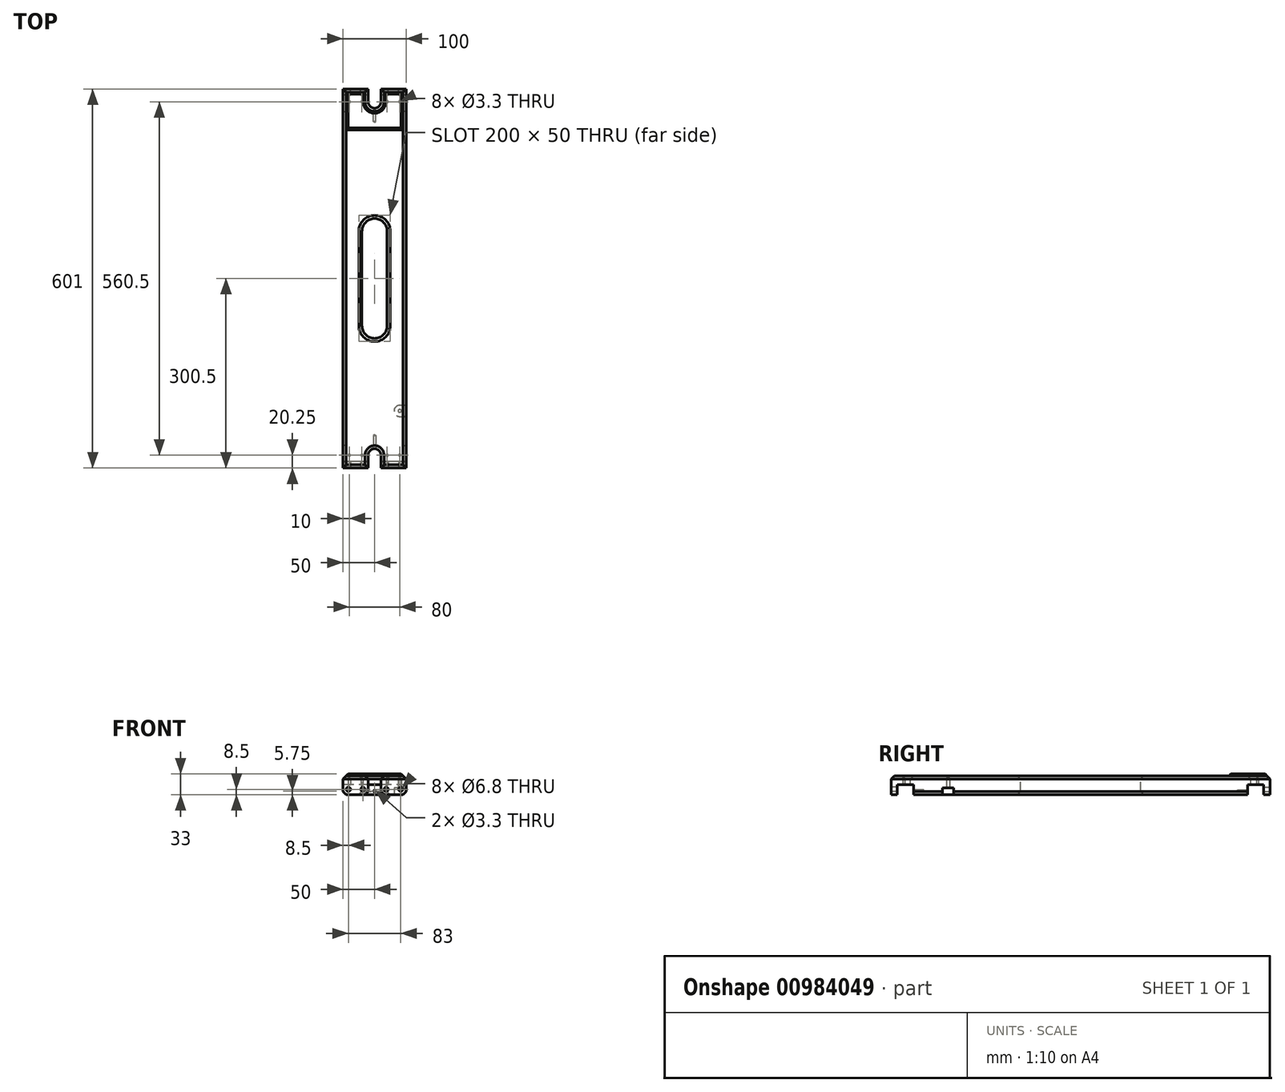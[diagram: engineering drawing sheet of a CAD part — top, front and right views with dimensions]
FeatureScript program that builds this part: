
annotation { "Feature Type Name" : "Feature", "Feature Type Description" : "" }
export const myFeature = defineFeature(function(context is Context, id is Id, definition is map)
    precondition{}
    {
        {
            var Q0;
            Q0=qCreatedBy(makeId("Right.planeOp"),FACE);
            var sketch = newSketch(context, id + "F0", { "sketchPlane" : qUnion([Q0])});
            skLineSegment(sketch, "E0", {"start": v(-300.5, -30) * mm, "end": v(-290.5, -30) * mm});
            skLineSegment(sketch, "E1", {"start": v(-290.5, -30) * mm, "end": v(-290.5, -14) * mm});
            skLineSegment(sketch, "E2", {"start": v(265, -30) * mm, "end": v(265, -14) * mm});
            skLineSegment(sketch, "E3", {"start": v(265, -14) * mm, "end": v(290.5, -14) * mm});
            skLineSegment(sketch, "E4", {"start": v(290.5, -14) * mm, "end": v(290.5, -30) * mm});
            skLineSegment(sketch, "E5", {"start": v(290.5, -30) * mm, "end": v(300.5, -30) * mm});
            skLineSegment(sketch, "E6", {"start": v(300.5, -30) * mm, "end": v(300.5, 0) * mm});
            skLineSegment(sketch, "E7", {"start": v(300.5, 0) * mm, "end": v(-300.5, 0) * mm});
            skLineSegment(sketch, "E8", {"start": v(-300.5, 0) * mm, "end": v(-300.5, -30) * mm});
            skLineSegment(sketch, "E9", {"start": v(-290.5, -14) * mm, "end": v(-265, -14) * mm});
            skLineSegment(sketch, "E10", {"start": v(-265, -14) * mm, "end": v(-265, -30) * mm});
            skLineSegment(sketch, "E11", {"start": v(-265, -30) * mm, "end": v(265, -30) * mm});
            skSolve(sketch);
        }
        {
            var Q0;
            Q0=makeQuery(id+"F0.imprint","IMPRINT",FACE,{"disambiguationData":[TD([[makeQuery(id+"F0.imprint","IMPRINT",EDGE,{"derivedFrom":sQuery(id+"F0.wireOp",EDGE,"E0")}),1.0]])]});
            extrude(context, id + "F1", {"entities" : qUnion([Q0]), "depth" : 100 * mm, "offsetDistance" : 25 * mm, "symmetric" : true});
        }
        {
            var Q0;
            {var subQ0=sQuery(id+"F0.wireOp",EDGE,"E7");Q0=makeQuery(id+"F2rq3QJmj17pkRO_1.boolean.opBoolean","MERGE",FACE,{"derivedFrom":[makeQuery(id+"F1.opExtrude","SWEPT_FACE",FACE,{"disambiguationData":[OSD([subQ0])]}),makeQuery(id+"F2rq3QJmj17pkRO_1.opExtrude","SWEPT_FACE",FACE,{"disambiguationData":[OSD([subQ0]),TDD([makeQuery(id+"F0.imprint","IMPRINT",EDGE,{"disambiguationData":[TD([[makeQuery(id+"F0.imprint","INTERSECT",VERTEX,{"derivedFrom":[sQuery(id+"F0.wireOp",EDGE,"E6"),subQ0]}),-1.0]])],"derivedFrom":subQ0})])]}),makeQuery(id+"F2rq3QJmj17pkRO_1.opExtrude","SWEPT_FACE",FACE,{"disambiguationData":[OSD([subQ0]),TDD([makeQuery(id+"F0.imprint","IMPRINT",EDGE,{"disambiguationData":[TD([[makeQuery(id+"F0.imprint","INTERSECT",VERTEX,{"derivedFrom":[subQ0,sQuery(id+"F0.wireOp",EDGE,"E8")]}),1.0]])],"derivedFrom":subQ0})])]})]});}
            var sketch = newSketch(context, id + "F2", { "sketchPlane" : qUnion([Q0])});
            skLineSegment(sketch, "E12.bottom", {"start": v(20, -75) * mm, "end": v(-20, -75) * mm});
            skLineSegment(sketch, "E12.top", {"start": v(20, 75) * mm, "end": v(-20, 75) * mm});
            skLineSegment(sketch, "E12.left", {"start": v(20, -75) * mm, "end": v(20, 75) * mm});
            skLineSegment(sketch, "E12.right", {"start": v(-20, -75) * mm, "end": v(-20, 75) * mm});
            skPoint(sketch, "E12.middle", {"position": v(0, 0) * mm});
            skCircle(sketch, "E13", {"center": v(0, 280) * mm, "radius": 10 * mm});
            skCircle(sketch, "E14", {"center": v(0, -280) * mm, "radius": 10 * mm});
            skLineSegment(sketch, "E15.bottom", {"start": v(-10, -280) * mm, "end": v(10, -280) * mm});
            skLineSegment(sketch, "E15.top", {"start": v(-10, -300.5) * mm, "end": v(10, -300.5) * mm});
            skLineSegment(sketch, "E15.left", {"start": v(-10, -280) * mm, "end": v(-10, -300.5) * mm});
            skLineSegment(sketch, "E15.right", {"start": v(10, -280) * mm, "end": v(10, -300.5) * mm});
            skLineSegment(sketch, "E16.bottom", {"start": v(-10, 280) * mm, "end": v(10, 280) * mm});
            skLineSegment(sketch, "E16.top", {"start": v(-10, 300.5) * mm, "end": v(10, 300.5) * mm});
            skLineSegment(sketch, "E16.left", {"start": v(-10, 280) * mm, "end": v(-10, 300.5) * mm});
            skLineSegment(sketch, "E16.right", {"start": v(10, 280) * mm, "end": v(10, 300.5) * mm});
            skCircle(sketch, "E17", {"center": v(0, 75) * mm, "radius": 20 * mm});
            skCircle(sketch, "E18", {"center": v(0, -75) * mm, "radius": 20 * mm});
            skSolve(sketch);
        }
        {
            var Q0;
            Q0 = qSketchRegion(id + "F2", true);
            extrude(context, id + "F3", {"entities" : qUnion([Q0]), "operationType" : NewBodyOperationType.REMOVE, "endBound" : BoundingType.THROUGH_ALL, "oppositeDirection" : true, "depth" : 25 * mm, "offsetDistance" : 25 * mm});
        }
        {
            var Q0;
            {var subQ1=sQuery(id+"F0.wireOp",EDGE,"E6");Q0=makeQuery(id+"F3.boolean.opBoolean","SPLIT",FACE,{"disambiguationData":[TD([makeQuery(id+"F3.opExtrude","SWEPT_FACE",FACE,{"disambiguationData":[OSD([sQuery(id+"F2.wireOp",EDGE,"E16.right")])]})])],"derivedFrom":makeQuery(id+"F1.opExtrude","SWEPT_FACE",FACE,{"disambiguationData":[OSD([subQ1])]})});}
            var sketch = newSketch(context, id + "F4", { "sketchPlane" : qUnion([Q0])});
            skLineSegment(sketch, "E19", {"start": v(-41.5, -21.5) * mm, "end": v(41.5, -21.5) * mm, "construction": true});
            skPoint(sketch, "E20", {"position": v(-18.5, -21.5) * mm});
            skPoint(sketch, "E21", {"position": v(18.5, -21.5) * mm});
            skLineSegment(sketch, "E22.0", {"start": v(-10, -14) * mm, "end": v(10, -14) * mm, "construction": true});
            skLineSegment(sketch, "E23", {"start": v(0, -14) * mm, "end": v(0, -24.25) * mm, "construction": true});
            skPoint(sketch, "E24", {"position": v(0, -24.25) * mm});
            skSolve(sketch);
        }
        {
            var Q0;
            {var subQ1=sQuery(id+"F0.wireOp",EDGE,"E8");Q0=makeQuery(id+"F3.boolean.opBoolean","SPLIT",FACE,{"disambiguationData":[TD([makeQuery(id+"F3.opExtrude","SWEPT_FACE",FACE,{"disambiguationData":[OSD([sQuery(id+"F2.wireOp",EDGE,"E15.left")])]})])],"derivedFrom":makeQuery(id+"F1.opExtrude","SWEPT_FACE",FACE,{"disambiguationData":[OSD([subQ1])]})});}
            var sketch = newSketch(context, id + "F5", { "sketchPlane" : qUnion([Q0])});
            skPoint(sketch, "E25.0", {"position": v(0, -24.25) * mm});
            skPoint(sketch, "E26.0", {"position": v(-18.5, -21.5) * mm});
            skPoint(sketch, "E27.0", {"position": v(18.5, -21.5) * mm});
            skPoint(sketch, "E28.0", {"position": v(41.5, -21.5) * mm});
            skPoint(sketch, "E29.0", {"position": v(-41.5, -21.5) * mm});
            skSolve(sketch);
        }
        {
            var Q0;
            Q0=sQuery(id+"F5.wireOp",VERTEX,"E29.0");
            var Q1;
            Q1=sQuery(id+"F5.wireOp",VERTEX,"E26.0");
            var Q2;
            Q2=sQuery(id+"F5.wireOp",VERTEX,"E27.0");
            var Q3;
            Q3=sQuery(id+"F5.wireOp",VERTEX,"E28.0");
            var Q4;
            Q4=sQuery(id+"F4.wireOp",VERTEX,"E19.start");
            var Q5;
            Q5=sQuery(id+"F4.wireOp",VERTEX,"E20");
            var Q6;
            Q6=sQuery(id+"F4.wireOp",VERTEX,"E21");
            var Q7;
            Q7=sQuery(id+"F4.wireOp",VERTEX,"E19.end");
            var Q8;
            Q8=makeQuery(id+"F1.opExtrude","SWEPT_BODY",BODY,{"disambiguationData":[OSD([sQuery(id+"F0.wireOp",EDGE,"E0"),sQuery(id+"F0.wireOp",EDGE,"E1"),sQuery(id+"F0.wireOp",EDGE,"E2"),sQuery(id+"F0.wireOp",EDGE,"E3"),sQuery(id+"F0.wireOp",EDGE,"E4"),sQuery(id+"F0.wireOp",EDGE,"E5"),sQuery(id+"F0.wireOp",EDGE,"E6"),sQuery(id+"F0.wireOp",EDGE,"E7"),sQuery(id+"F0.wireOp",EDGE,"E8"),sQuery(id+"F0.wireOp",EDGE,"E9"),sQuery(id+"F0.wireOp",EDGE,"E10"),sQuery(id+"F0.wireOp",EDGE,"E11")])]});
            hole(context, id + "F6", {"style" : HoleStyle.SIMPLE, "endStyle" : HoleEndStyle.BLIND, "standardTappedOrClearance" : lookupTablePath({ "standard" : "ISO", "engagement" : "75%", "pitch" : "1.25 mm", "size" : "M8", "type" : "Tapped" }), "standardBlindInLast" : lookupTablePath({ "standard" : "ISO", "fit" : "Normal", "engagement" : "75%", "pitch" : "1.25 mm", "size" : "M8", "type" : "Clearance & tapped" }), "holeDiameter" : 6.8 * mm, "majorDiameter" : 8 * mm, "showTappedDepth" : true, "holeDepth" : 13.75 * mm, "tappedDepth" : 10 * mm, "tapClearance" : 3, "startFromSketch" : true, "locations" : qUnion([Q0, Q1, Q2, Q3, Q4, Q5, Q6, Q7]), "scope" : qUnion([Q8])});
        }
        {
            var Q0;
            Q0=sQuery(id+"F5.wireOp",VERTEX,"E25.0");
            var Q1;
            Q1=sQuery(id+"F4.wireOp",VERTEX,"E24");
            var Q2;
            Q2=makeQuery(id+"F1.opExtrude","SWEPT_BODY",BODY,{"disambiguationData":[OSD([sQuery(id+"F0.wireOp",EDGE,"E0"),sQuery(id+"F0.wireOp",EDGE,"E1"),sQuery(id+"F0.wireOp",EDGE,"E2"),sQuery(id+"F0.wireOp",EDGE,"E3"),sQuery(id+"F0.wireOp",EDGE,"E4"),sQuery(id+"F0.wireOp",EDGE,"E5"),sQuery(id+"F0.wireOp",EDGE,"E6"),sQuery(id+"F0.wireOp",EDGE,"E7"),sQuery(id+"F0.wireOp",EDGE,"E8"),sQuery(id+"F0.wireOp",EDGE,"E9"),sQuery(id+"F0.wireOp",EDGE,"E10"),sQuery(id+"F0.wireOp",EDGE,"E11")])]});
            hole(context, id + "F7", {"style" : HoleStyle.SIMPLE, "endStyle" : HoleEndStyle.BLIND, "standardTappedOrClearance" : lookupTablePath({ "standard" : "ISO", "engagement" : "75%", "pitch" : "0.7 mm", "size" : "M4", "type" : "Tapped" }), "standardBlindInLast" : lookupTablePath({ "standard" : "ISO", "fit" : "Normal", "engagement" : "75%", "pitch" : "0.7 mm", "size" : "M4", "type" : "Clearance & tapped" }), "holeDiameter" : 3.3 * mm, "majorDiameter" : 4 * mm, "showTappedDepth" : true, "holeDepth" : 16.1 * mm, "tappedDepth" : 14 * mm, "tapClearance" : 3, "locations" : qUnion([Q0, Q1]), "scope" : qUnion([Q2])});
        }
        {
            var Q0;
            Q0=makeQuery(id+"F1.opExtrude","SWEPT_FACE",FACE,{"disambiguationData":[OSD([sQuery(id+"F0.wireOp",EDGE,"E3")])]});
            var sketch = newSketch(context, id + "F8", { "sketchPlane" : qUnion([Q0])});
            skLineSegment(sketch, "E30", {"start": v(-40, 280.25) * mm, "end": v(40, 280.25) * mm, "construction": true});
            skPoint(sketch, "E31", {"position": v(-20, 280.25) * mm});
            skPoint(sketch, "E32", {"position": v(20, 280.25) * mm});
            skLineSegment(sketch, "E33", {"start": v(-40, -280.25) * mm, "end": v(40, -280.25) * mm, "construction": true});
            skPoint(sketch, "E34", {"position": v(-20, -280.25) * mm});
            skPoint(sketch, "E35", {"position": v(20, -280.25) * mm});
            skPoint(sketch, "E36", {"position": v(0, 280.25) * mm});
            skPoint(sketch, "E37", {"position": v(0, -280.25) * mm});
            skSolve(sketch);
        }
        {
            var Q0;
            Q0=sQuery(id+"F8.wireOp",VERTEX,"E30.start");
            var Q1;
            Q1=sQuery(id+"F8.wireOp",VERTEX,"E31");
            var Q2;
            Q2=sQuery(id+"F8.wireOp",VERTEX,"E32");
            var Q3;
            Q3=sQuery(id+"F8.wireOp",VERTEX,"E30.end");
            var Q4;
            Q4=sQuery(id+"F8.wireOp",VERTEX,"E33.start");
            var Q5;
            Q5=sQuery(id+"F8.wireOp",VERTEX,"E34");
            var Q6;
            Q6=sQuery(id+"F8.wireOp",VERTEX,"E35");
            var Q7;
            Q7=sQuery(id+"F8.wireOp",VERTEX,"E33.end");
            var Q8;
            Q8=makeQuery(id+"F1.opExtrude","SWEPT_BODY",BODY,{"disambiguationData":[OSD([sQuery(id+"F0.wireOp",EDGE,"E0"),sQuery(id+"F0.wireOp",EDGE,"E1"),sQuery(id+"F0.wireOp",EDGE,"E2"),sQuery(id+"F0.wireOp",EDGE,"E3"),sQuery(id+"F0.wireOp",EDGE,"E4"),sQuery(id+"F0.wireOp",EDGE,"E5"),sQuery(id+"F0.wireOp",EDGE,"E6"),sQuery(id+"F0.wireOp",EDGE,"E7"),sQuery(id+"F0.wireOp",EDGE,"E8"),sQuery(id+"F0.wireOp",EDGE,"E9"),sQuery(id+"F0.wireOp",EDGE,"E10"),sQuery(id+"F0.wireOp",EDGE,"E11")])]});
            hole(context, id + "F9", {"style" : HoleStyle.SIMPLE, "endStyle" : HoleEndStyle.BLIND, "standardTappedOrClearance" : lookupTablePath({ "standard" : "ISO", "engagement" : "75%", "pitch" : "0.7 mm", "size" : "M4", "type" : "Tapped" }), "standardBlindInLast" : lookupTablePath({ "standard" : "ISO", "fit" : "Normal", "engagement" : "75%", "pitch" : "0.7 mm", "size" : "M4", "type" : "Clearance & tapped" }), "holeDiameter" : 3.3 * mm, "majorDiameter" : 4 * mm, "showTappedDepth" : true, "holeDepth" : 10.1 * mm, "tappedDepth" : 8 * mm, "tapClearance" : 3, "startFromSketch" : true, "locations" : qUnion([Q0, Q1, Q2, Q3, Q4, Q5, Q6, Q7]), "scope" : qUnion([Q8])});
        }
        {
            var Q0;
            Q0=makeQuery(id+"F1.opExtrude","SWEPT_FACE",FACE,{"disambiguationData":[OSD([sQuery(id+"F0.wireOp",EDGE,"E11")])]});
            var sketch = newSketch(context, id + "F10", { "sketchPlane" : qUnion([Q0])});
            skPoint(sketch, "E38", {"position": v(40, 210) * mm});
            skCircle(sketch, "E39", {"center": v(40, 210) * mm, "radius": 9 * mm});
            skLineSegment(sketch, "E40.bottom", {"start": v(40, 219) * mm, "end": v(50, 219) * mm});
            skLineSegment(sketch, "E40.top", {"start": v(40, 201) * mm, "end": v(50, 201) * mm});
            skLineSegment(sketch, "E40.left", {"start": v(40, 219) * mm, "end": v(40, 201) * mm});
            skLineSegment(sketch, "E40.right", {"start": v(50, 219) * mm, "end": v(50, 201) * mm});
            skSolve(sketch);
        }
        {
            var Q0;
            {var subQ0=sQuery(id+"F10.wireOp",EDGE,"E40.left");Q0=makeQuery(id+"F10.imprint","IMPRINT",FACE,{"disambiguationData":[TD([[makeQuery(id+"F10.imprint","IMPRINT",EDGE,{"derivedFrom":subQ0}),-1.0]])]});}
            var Q1;
            {var subQ0=sQuery(id+"F10.wireOp",EDGE,"E40.left");Q1=makeQuery(id+"F10.imprint","IMPRINT",FACE,{"disambiguationData":[TD([[makeQuery(id+"F10.imprint","IMPRINT",EDGE,{"derivedFrom":subQ0}),1.0]])]});}
            var Q2;
            {var subQ0=sQuery(id+"F10.wireOp",EDGE,"E40.bottom");Q2=makeQuery(id+"F10.imprint","IMPRINT",FACE,{"disambiguationData":[TD([[makeQuery(id+"F10.imprint","IMPRINT",EDGE,{"derivedFrom":subQ0}),-1.0]])]});}
            var Q3;
            {var subQ0=sQuery(id+"F10.wireOp",EDGE,"E40.top");Q3=makeQuery(id+"F10.imprint","IMPRINT",FACE,{"disambiguationData":[TD([[makeQuery(id+"F10.imprint","IMPRINT",EDGE,{"derivedFrom":subQ0}),1.0]])]});}
            extrude(context, id + "F11", {"entities" : qUnion([Q0, Q1, Q2, Q3]), "operationType" : NewBodyOperationType.REMOVE, "oppositeDirection" : true, "depth" : 11 * mm, "offsetDistance" : 25 * mm});
        }
        {
            var Q0;
            Q0=sQuery(id+"F10.wireOp",VERTEX,"E38");
            var Q1;
            Q1=makeQuery(id+"F1.opExtrude","SWEPT_BODY",BODY,{"disambiguationData":[OSD([sQuery(id+"F0.wireOp",EDGE,"E0"),sQuery(id+"F0.wireOp",EDGE,"E1"),sQuery(id+"F0.wireOp",EDGE,"E2"),sQuery(id+"F0.wireOp",EDGE,"E3"),sQuery(id+"F0.wireOp",EDGE,"E4"),sQuery(id+"F0.wireOp",EDGE,"E5"),sQuery(id+"F0.wireOp",EDGE,"E6"),sQuery(id+"F0.wireOp",EDGE,"E7"),sQuery(id+"F0.wireOp",EDGE,"E8"),sQuery(id+"F0.wireOp",EDGE,"E9"),sQuery(id+"F0.wireOp",EDGE,"E10"),sQuery(id+"F0.wireOp",EDGE,"E11")])]});
            hole(context, id + "F12", {"style" : HoleStyle.SIMPLE, "endStyle" : HoleEndStyle.BLIND, "standardTappedOrClearance" : lookupTablePath({ "standard" : "ISO", "engagement" : "75%", "pitch" : "1 mm", "size" : "M6", "type" : "Tapped" }), "standardBlindInLast" : lookupTablePath({ "standard" : "ISO", "fit" : "Normal", "engagement" : "75%", "pitch" : "1 mm", "size" : "M6", "type" : "Clearance & tapped" }), "holeDiameter" : 5 * mm, "majorDiameter" : 6 * mm, "showTappedDepth" : true, "holeDepth" : 15 * mm, "tappedDepth" : 12 * mm, "tapClearance" : 3, "locations" : qUnion([Q0]), "scope" : qUnion([Q1])});
        }
        {
            var Q0;
            Q0=makeQuery(id+"F3.boolean.opBoolean","INTERSECT",EDGE,{"derivedFrom":[makeQuery(id+"F1.opExtrude","SWEPT_FACE",FACE,{"disambiguationData":[OSD([sQuery(id+"F0.wireOp",EDGE,"E0")])]}),makeQuery(id+"F3.opExtrude","SWEPT_FACE",FACE,{"disambiguationData":[OSD([sQuery(id+"F2.wireOp",EDGE,"E15.right")])]})]});
            var Q1;
            Q1=makeQuery(id+"F1.opExtrude","CAP_EDGE",EDGE,{"disambiguationData":[OSD([sQuery(id+"F0.wireOp",EDGE,"E0")])],"isStart":false});
            var Q2;
            Q2=makeQuery(id+"F1.opExtrude","CAP_EDGE",EDGE,{"disambiguationData":[OSD([sQuery(id+"F0.wireOp",EDGE,"E0")])],"isStart":true});
            var Q3;
            Q3=makeQuery(id+"F3.boolean.opBoolean","INTERSECT",EDGE,{"derivedFrom":[makeQuery(id+"F1.opExtrude","SWEPT_FACE",FACE,{"disambiguationData":[OSD([sQuery(id+"F0.wireOp",EDGE,"E0")])]}),makeQuery(id+"F3.opExtrude","SWEPT_FACE",FACE,{"disambiguationData":[OSD([sQuery(id+"F2.wireOp",EDGE,"E15.left")])]})]});
            var Q4;
            Q4=makeQuery(id+"F1.opExtrude","CAP_EDGE",EDGE,{"disambiguationData":[OSD([sQuery(id+"F0.wireOp",EDGE,"E5")])],"isStart":true});
            var Q5;
            Q5=makeQuery(id+"F3.boolean.opBoolean","INTERSECT",EDGE,{"derivedFrom":[makeQuery(id+"F1.opExtrude","SWEPT_FACE",FACE,{"disambiguationData":[OSD([sQuery(id+"F0.wireOp",EDGE,"E5")])]}),makeQuery(id+"F3.opExtrude","SWEPT_FACE",FACE,{"disambiguationData":[OSD([sQuery(id+"F2.wireOp",EDGE,"E16.left")])]})]});
            var Q6;
            Q6=makeQuery(id+"F1.opExtrude","CAP_EDGE",EDGE,{"disambiguationData":[OSD([sQuery(id+"F0.wireOp",EDGE,"E5")])],"isStart":false});
            var Q7;
            Q7=makeQuery(id+"F3.boolean.opBoolean","INTERSECT",EDGE,{"derivedFrom":[makeQuery(id+"F1.opExtrude","SWEPT_FACE",FACE,{"disambiguationData":[OSD([sQuery(id+"F0.wireOp",EDGE,"E5")])]}),makeQuery(id+"F3.opExtrude","SWEPT_FACE",FACE,{"disambiguationData":[OSD([sQuery(id+"F2.wireOp",EDGE,"E16.right")])]})]});
            fillet(context, id + "F13", {"entities" : qUnion([Q0, Q1, Q2, Q3, Q4, Q5, Q6, Q7]), "radius" : 8 * mm, "tangentPropagation" : true, "allowEdgeOverflow" : false});
        }
        {
            var Q0;
            Q0=makeQuery(id+"F3.boolean.opBoolean","COPY",EDGE,{"derivedFrom":makeQuery(id+"F3.opExtrude","SWEPT_EDGE",EDGE,{"disambiguationData":[OSD([sQuery(id+"F0.wireOp",EDGE,"E6"),sQuery(id+"F0.wireOp",EDGE,"E7"),sQuery(id+"F2.wireOp",EDGE,"E16.top"),sQuery(id+"F2.wireOp",EDGE,"E16.right")])]})});
            var Q1;
            Q1=makeQuery(id+"F3.boolean.opBoolean","COPY",EDGE,{"derivedFrom":makeQuery(id+"F3.opExtrude","SWEPT_EDGE",EDGE,{"disambiguationData":[OSD([sQuery(id+"F0.wireOp",EDGE,"E6"),sQuery(id+"F0.wireOp",EDGE,"E7"),sQuery(id+"F2.wireOp",EDGE,"E16.top"),sQuery(id+"F2.wireOp",EDGE,"E16.left")])]})});
            var Q2;
            Q2=makeQuery(id+"F3.boolean.opBoolean","COPY",EDGE,{"derivedFrom":makeQuery(id+"F3.opExtrude","SWEPT_EDGE",EDGE,{"disambiguationData":[OSD([sQuery(id+"F0.wireOp",EDGE,"E7"),sQuery(id+"F0.wireOp",EDGE,"E8"),sQuery(id+"F2.wireOp",EDGE,"E15.top"),sQuery(id+"F2.wireOp",EDGE,"E15.right")])]})});
            var Q3;
            Q3=makeQuery(id+"F3.boolean.opBoolean","COPY",EDGE,{"derivedFrom":makeQuery(id+"F3.opExtrude","SWEPT_EDGE",EDGE,{"disambiguationData":[OSD([sQuery(id+"F0.wireOp",EDGE,"E7"),sQuery(id+"F0.wireOp",EDGE,"E8"),sQuery(id+"F2.wireOp",EDGE,"E15.top"),sQuery(id+"F2.wireOp",EDGE,"E15.left")])]})});
            var Q4;
            Q4=makeQuery(id+"F11.boolean.opBoolean","COPY",EDGE,{"derivedFrom":makeQuery(id+"F11.opExtrude","SWEPT_EDGE",EDGE,{"disambiguationData":[OSD([sQuery(id+"F0.wireOp",EDGE,"E11"),sQuery(id+"F10.wireOp",EDGE,"E40.bottom"),sQuery(id+"F10.wireOp",EDGE,"E40.right")])]})});
            var Q5;
            Q5=makeQuery(id+"F11.boolean.opBoolean","COPY",EDGE,{"derivedFrom":makeQuery(id+"F11.opExtrude","SWEPT_EDGE",EDGE,{"disambiguationData":[OSD([sQuery(id+"F0.wireOp",EDGE,"E11"),sQuery(id+"F10.wireOp",EDGE,"E40.top"),sQuery(id+"F10.wireOp",EDGE,"E40.right")])]})});
            var Q6;
            Q6=makeQuery(id+"F1.opExtrude","CAP_EDGE",EDGE,{"disambiguationData":[OSD([sQuery(id+"F0.wireOp",EDGE,"E11")])],"isStart":true});
            var Q7;
            {var subQ0=sQuery(id+"F0.wireOp",EDGE,"E11");var subQ1=sQuery(id+"F0.wireOp",EDGE,"E10");Q7=makeQuery(id+"F11.boolean.opBoolean","SPLIT",EDGE,{"disambiguationData":[TD([makeQuery(id+"F1.opExtrude","SWEPT_FACE",FACE,{"disambiguationData":[OSD([subQ1])]})])],"derivedFrom":makeQuery(id+"F1.opExtrude","CAP_EDGE",EDGE,{"disambiguationData":[OSD([subQ0])],"isStart":false})});}
            var Q8;
            {var subQ0=sQuery(id+"F0.wireOp",EDGE,"E11");var subQ1=sQuery(id+"F0.wireOp",EDGE,"E2");Q8=makeQuery(id+"F11.boolean.opBoolean","SPLIT",EDGE,{"disambiguationData":[TD([makeQuery(id+"F1.opExtrude","SWEPT_FACE",FACE,{"disambiguationData":[OSD([subQ1])]})])],"derivedFrom":makeQuery(id+"F1.opExtrude","CAP_EDGE",EDGE,{"disambiguationData":[OSD([subQ0])],"isStart":false})});}
            var Q9;
            Q9=makeQuery(id+"F3.boolean.opBoolean","INTERSECT",EDGE,{"derivedFrom":[makeQuery(id+"F1.opExtrude","SWEPT_FACE",FACE,{"disambiguationData":[OSD([sQuery(id+"F0.wireOp",EDGE,"E11")])]}),makeQuery(id+"F3.opExtrude","SWEPT_FACE",FACE,{"disambiguationData":[OSD([sQuery(id+"F2.wireOp",EDGE,"E17")])]})]});
            var Q10;
            Q10=makeQuery(id+"F11.boolean.opBoolean","COPY",EDGE,{"derivedFrom":makeQuery(id+"F11.opExtrude","CAP_EDGE",EDGE,{"disambiguationData":[OSD([sQuery(id+"F10.wireOp",EDGE,"E39")])],"isStart":true})});
            var Q11;
            {var subQ0=sQuery(id+"F0.wireOp",EDGE,"E8");var subQ1=sQuery(id+"F0.wireOp",EDGE,"E7");Q11=makeQuery(id+"F3.boolean.opBoolean","SPLIT",EDGE,{"disambiguationData":[TD([makeQuery(id+"F3.opExtrude","SWEPT_FACE",FACE,{"disambiguationData":[OSD([sQuery(id+"F2.wireOp",EDGE,"E15.left")])]})])],"derivedFrom":makeQuery(id+"F1.opExtrude","SWEPT_EDGE",EDGE,{"disambiguationData":[OSD([subQ1,subQ0])]})});}
            var Q12;
            {var subQ0=sQuery(id+"F0.wireOp",EDGE,"E8");var subQ1=sQuery(id+"F0.wireOp",EDGE,"E7");Q12=makeQuery(id+"F3.boolean.opBoolean","SPLIT",EDGE,{"disambiguationData":[TD([makeQuery(id+"F3.opExtrude","SWEPT_FACE",FACE,{"disambiguationData":[OSD([sQuery(id+"F2.wireOp",EDGE,"E15.right")])]})])],"derivedFrom":makeQuery(id+"F1.opExtrude","SWEPT_EDGE",EDGE,{"disambiguationData":[OSD([subQ1,subQ0])]})});}
            var Q13;
            Q13=makeQuery(id+"F3.boolean.opBoolean","COPY",EDGE,{"derivedFrom":makeQuery(id+"F3.opExtrude","CAP_EDGE",EDGE,{"disambiguationData":[OSD([sQuery(id+"F2.wireOp",EDGE,"E15.right")])],"isStart":true})});
            var Q14;
            Q14=makeQuery(id+"F1.opExtrude","SWEPT_FACE",FACE,{"disambiguationData":[OSD([sQuery(id+"F0.wireOp",EDGE,"E7")])]});
            chamfer(context, id + "F14", {"entities" : qUnion([Q0, Q1, Q2, Q3, Q4, Q5, Q6, Q7, Q8, Q9, Q10, Q11, Q12, Q13, Q14]), "width" : 5 * mm, "tangentPropagation" : true});
        }
        {
            var Q0;
            Q0=makeQuery(id+"F1.opExtrude","SWEPT_FACE",FACE,{"disambiguationData":[OSD([sQuery(id+"F0.wireOp",EDGE,"E7")])]});
            var sketch = newSketch(context, id + "F15", { "sketchPlane" : qUnion([Q0])});
            skLineSegment(sketch, "E41.0", {"start": v(-45, 295.5) * mm, "end": v(-45, 235.5) * mm});
            skLineSegment(sketch, "E41.1", {"start": v(-15, 295.5) * mm, "end": v(-45, 295.5) * mm});
            skLineSegment(sketch, "E41.2", {"start": v(-15, 280) * mm, "end": v(-15, 295.5) * mm});
            skLineSegment(sketch, "E41.3", {"start": v(45, 235.5) * mm, "end": v(45, 295.5) * mm});
            skLineSegment(sketch, "E41.4", {"start": v(45, 295.5) * mm, "end": v(15, 295.5) * mm});
            skLineSegment(sketch, "E41.5", {"start": v(15, 295.5) * mm, "end": v(15, 280) * mm});
            skArc(sketch, "E41.6", {"start": v(15, 280) * mm, "mid": v(0, 265) * mm, "end": v(-15, 280) * mm});
            skLineSegment(sketch, "E42", {"start": v(-45, 235.5) * mm, "end": v(45, 235.5) * mm});
            skSolve(sketch);
        }
        {
            var Q0;
            Q0=makeQuery(id+"F15.imprint","IMPRINT",FACE,{"disambiguationData":[TD([[makeQuery(id+"F15.imprint","IMPRINT",EDGE,{"derivedFrom":sQuery(id+"F15.wireOp",EDGE,"E41.0")}),1.0]])]});
            extrude(context, id + "F16", {"entities" : qUnion([Q0]), "depth" : 3 * mm, "offsetDistance" : 25 * mm});
        }
        {
            var Q0;
            Q0=makeQuery(id+"F16.opExtrude","CAP_EDGE",EDGE,{"disambiguationData":[OSD([sQuery(id+"F15.wireOp",EDGE,"E42")])],"isStart":false});
            var Q1;
            Q1=makeQuery(id+"F16.opExtrude","CAP_EDGE",EDGE,{"disambiguationData":[OSD([sQuery(id+"F15.wireOp",EDGE,"E41.6")])],"isStart":false});
            var Q2;
            Q2=makeQuery(id+"F16.opExtrude","CAP_EDGE",EDGE,{"disambiguationData":[OSD([sQuery(id+"F15.wireOp",EDGE,"E41.3")])],"isStart":false});
            var Q3;
            Q3=makeQuery(id+"F16.opExtrude","CAP_FACE",FACE,{"disambiguationData":[OSD([sQuery(id+"F15.wireOp",EDGE,"E41.0"),sQuery(id+"F15.wireOp",EDGE,"E41.1"),sQuery(id+"F15.wireOp",EDGE,"E41.2"),sQuery(id+"F15.wireOp",EDGE,"E41.3"),sQuery(id+"F15.wireOp",EDGE,"E41.4"),sQuery(id+"F15.wireOp",EDGE,"E41.5"),sQuery(id+"F15.wireOp",EDGE,"E41.6"),sQuery(id+"F15.wireOp",EDGE,"E42")])],"isStart":false});
            chamfer(context, id + "F17", {"entities" : qUnion([Q0, Q1, Q2, Q3]), "width" : 3 * mm, "tangentPropagation" : true});
        }
    });
